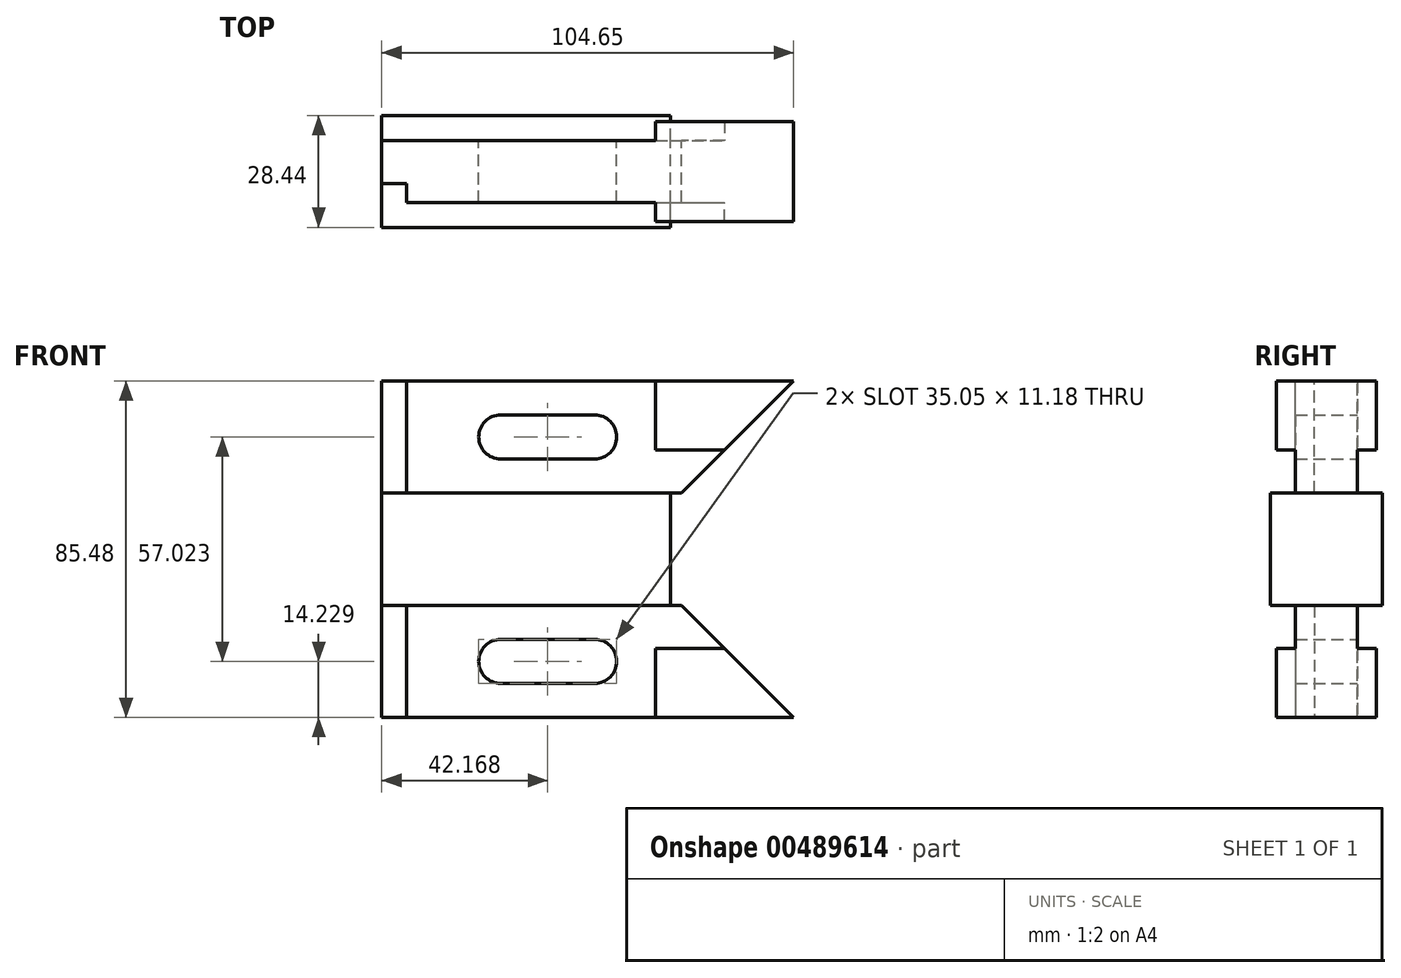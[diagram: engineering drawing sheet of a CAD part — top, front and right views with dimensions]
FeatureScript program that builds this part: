
annotation { "Feature Type Name" : "Feature", "Feature Type Description" : "" }
export const myFeature = defineFeature(function(context is Context, id is Id, definition is map)
    precondition{}
    {
        {
            var Q0;
            Q0=qCreatedBy(makeId("Front.planeOp"),FACE);
            var sketch = newSketch(context, id + "F0", { "sketchPlane" : qUnion([Q0])});
            skLineSegment(sketch, "E0.top", {"start": v(0, 14.29) * mm, "end": v(-73.4, 14.29) * mm});
            skLineSegment(sketch, "E1", {"start": v(-73.4, 14.29) * mm, "end": v(-73.4, 42.74) * mm});
            skLineSegment(sketch, "E2", {"start": v(-73.4, 42.74) * mm, "end": v(31.24, 42.74) * mm});
            skLineSegment(sketch, "E3", {"start": v(31.24, 42.74) * mm, "end": v(2.8, 14.29) * mm});
            skLineSegment(sketch, "E4", {"start": v(-67.06, 42.74) * mm, "end": v(-67.06, 14.29) * mm});
            skLineSegment(sketch, "E5", {"start": v(0, 14.29) * mm, "end": v(2.8, 14.29) * mm});
            skArc(sketch, "E6.0.startCap", {"start": v(-43.18, 22.92) * mm, "mid": v(-48.77, 28.51) * mm, "end": v(-43.18, 34.1) * mm});
            skArc(sketch, "E6.0.endCap", {"start": v(-19.3, 34.1) * mm, "mid": v(-13.72, 28.51) * mm, "end": v(-19.3, 22.92) * mm});
            skLineSegment(sketch, "E6.0.left", {"start": v(-43.18, 34.1) * mm, "end": v(-19.3, 34.1) * mm});
            skLineSegment(sketch, "E6.0.right", {"start": v(-43.18, 22.92) * mm, "end": v(-19.3, 22.92) * mm});
            skLineSegment(sketch, "E7", {"start": v(-48.77, 28.51) * mm, "end": v(-13.72, 28.51) * mm, "construction": true});
            skLineSegment(sketch, "E8", {"start": v(-73.4, 28.51) * mm, "end": v(-48.77, 28.51) * mm, "construction": true});
            skPoint(sketch, "E9", {"position": v(-67.06, 42.74) * mm});
            skPoint(sketch, "E10", {"position": v(-73.4, 42.74) * mm});
            skLineSegment(sketch, "E11.bottom", {"start": v(-73.4, 14.29) * mm, "end": v(0, 14.29) * mm});
            skLineSegment(sketch, "E11.top", {"start": v(-73.4, 0) * mm, "end": v(0, 0) * mm});
            skLineSegment(sketch, "E11.left", {"start": v(-73.4, 14.29) * mm, "end": v(-73.4, 0) * mm});
            skLineSegment(sketch, "E11.right", {"start": v(0, 14.29) * mm, "end": v(0, 0) * mm});
            skLineSegment(sketch, "E12", {"start": v(-73.4, 42.74) * mm, "end": v(-3.58, 42.74) * mm, "construction": true});
            skLineSegment(sketch, "E13", {"start": v(-3.58, 42.74) * mm, "end": v(-3.58, 25.2) * mm});
            skLineSegment(sketch, "E14", {"start": v(13.72, 25.2) * mm, "end": v(-3.58, 25.2) * mm});
            skSolve(sketch);
        }
        {
            var Q0;
            Q0 = qSketchRegion(id + "F0", true);
            extrude(context, id + "F1", {"entities" : qUnion([Q0]), "endBound" : BoundingType.SYMMETRIC, "depth" : 28.45 * mm});
        }
        {
            var Q0;
            Q0=makeQuery(id+"F1.opExtrude","SWEPT_FACE",FACE,{"disambiguationData":[OSD([sQuery(id+"F0.wireOp",EDGE,"E2")])]});
            var sketch = newSketch(context, id + "F2", { "sketchPlane" : qUnion([Q0])});
            skLineSegment(sketch, "E15.bottom", {"start": v(-73.4, 14.22) * mm, "end": v(-3.8, 14.22) * mm});
            skLineSegment(sketch, "E15.top", {"start": v(-73.4, 7.87) * mm, "end": v(-3.8, 7.87) * mm});
            skLineSegment(sketch, "E15.left", {"start": v(-73.4, 14.22) * mm, "end": v(-73.4, 7.87) * mm});
            skLineSegment(sketch, "E15.right", {"start": v(-3.8, 14.22) * mm, "end": v(-3.8, 7.87) * mm});
            skLineSegment(sketch, "E16.bottom", {"start": v(0, 14.22) * mm, "end": v(-3.8, 14.22) * mm});
            skLineSegment(sketch, "E16.top", {"start": v(0, 12.7) * mm, "end": v(-3.8, 12.7) * mm});
            skLineSegment(sketch, "E16.left", {"start": v(0, 14.22) * mm, "end": v(0, 12.7) * mm});
            skLineSegment(sketch, "E16.right", {"start": v(-3.8, 14.22) * mm, "end": v(-3.8, 12.7) * mm});
            skLineSegment(sketch, "E17.MirrorCS", {"start": v(0, -14.22) * mm, "end": v(0, -12.7) * mm});
            skLineSegment(sketch, "E18.MirrorCS", {"start": v(-3.8, -14.22) * mm, "end": v(-3.8, -12.7) * mm});
            skLineSegment(sketch, "E19.MirrorCS", {"start": v(-73.4, -14.22) * mm, "end": v(-3.8, -14.22) * mm});
            skLineSegment(sketch, "E20.MirrorCS", {"start": v(-73.4, -7.87) * mm, "end": v(-3.8, -7.87) * mm});
            skLineSegment(sketch, "E21.MirrorCS", {"start": v(-73.4, -14.22) * mm, "end": v(-73.4, -7.87) * mm});
            skLineSegment(sketch, "E22.MirrorCS", {"start": v(-3.8, -14.22) * mm, "end": v(-3.8, -7.87) * mm});
            skLineSegment(sketch, "E23.MirrorCS", {"start": v(0, -12.7) * mm, "end": v(-3.8, -12.7) * mm});
            skLineSegment(sketch, "E24.MirrorCS", {"start": v(0, -14.22) * mm, "end": v(-3.8, -14.22) * mm});
            skLineSegment(sketch, "E25.bottom", {"start": v(-73.4, -7.87) * mm, "end": v(-67.06, -7.87) * mm});
            skLineSegment(sketch, "E25.top", {"start": v(-73.4, -3.05) * mm, "end": v(-67.06, -3.05) * mm});
            skLineSegment(sketch, "E25.left", {"start": v(-73.4, -7.87) * mm, "end": v(-73.4, -3.05) * mm});
            skLineSegment(sketch, "E25.right", {"start": v(-67.06, -7.87) * mm, "end": v(-67.06, -3.05) * mm});
            skSolve(sketch);
        }
        {
            var Q0;
            Q0=makeQuery(id+"F1.opExtrude","SWEPT_FACE",FACE,{"disambiguationData":[OSD([sQuery(id+"F0.wireOp",EDGE,"E11.right")])]});
            var sketch = newSketch(context, id + "F3", { "sketchPlane" : qUnion([Q0])});
            skLineSegment(sketch, "E26.bottom", {"start": v(-14.22, 14.29) * mm, "end": v(-12.7, 14.29) * mm});
            skLineSegment(sketch, "E26.top", {"start": v(-14.22, 42.74) * mm, "end": v(-12.7, 42.74) * mm});
            skLineSegment(sketch, "E26.left", {"start": v(-14.22, 14.29) * mm, "end": v(-14.22, 42.74) * mm});
            skLineSegment(sketch, "E26.right", {"start": v(-12.7, 14.29) * mm, "end": v(-12.7, 42.74) * mm});
            skLineSegment(sketch, "E27.bottom", {"start": v(14.22, 14.29) * mm, "end": v(12.7, 14.29) * mm});
            skLineSegment(sketch, "E27.top", {"start": v(14.22, 42.74) * mm, "end": v(12.7, 42.74) * mm});
            skLineSegment(sketch, "E27.left", {"start": v(14.22, 14.29) * mm, "end": v(14.22, 42.74) * mm});
            skLineSegment(sketch, "E27.right", {"start": v(12.7, 14.29) * mm, "end": v(12.7, 42.74) * mm});
            skLineSegment(sketch, "E28", {"start": v(7.87, 25.2) * mm, "end": v(7.87, 14.29) * mm});
            skLineSegment(sketch, "E29", {"start": v(-7.87, 14.29) * mm, "end": v(-7.87, 25.2) * mm});
            skLineSegment(sketch, "E30.bottom", {"start": v(-12.7, 14.29) * mm, "end": v(-7.87, 14.29) * mm});
            skLineSegment(sketch, "E30.top", {"start": v(-12.7, 25.2) * mm, "end": v(-7.87, 25.2) * mm});
            skLineSegment(sketch, "E30.left", {"start": v(-12.7, 14.29) * mm, "end": v(-12.7, 25.2) * mm});
            skLineSegment(sketch, "E31.bottom", {"start": v(12.7, 14.29) * mm, "end": v(7.87, 14.29) * mm});
            skLineSegment(sketch, "E31.top", {"start": v(12.7, 25.2) * mm, "end": v(7.87, 25.2) * mm});
            skLineSegment(sketch, "E31.left", {"start": v(12.7, 14.29) * mm, "end": v(12.7, 25.2) * mm});
            skLineSegment(sketch, "E31.right", {"start": v(7.87, 14.29) * mm, "end": v(7.87, 25.2) * mm});
            skSolve(sketch);
        }
        {
            var Q0;
            Q0 = qSketchRegion(id + "F3", true);
            extrude(context, id + "F4", {"entities" : qUnion([Q0]), "operationType" : NewBodyOperationType.REMOVE, "endBound" : BoundingType.THROUGH_ALL, "oppositeDirection" : true, "depth" : 25.4 * mm, "hasSecondDirection" : true, "secondDirectionBound" : SecondDirectionBoundingType.THROUGH_ALL, "secondDirectionOppositeDirection" : false, "secondDirectionDepth" : 25.4 * mm});
        }
        {
            var Q0;
            Q0 = qSketchRegion(id + "F2", true);
            var Q1;
            Q1=makeQuery(id+"F4.boolean.opBoolean","COPY",FACE,{"derivedFrom":makeQuery(id+"F4.opExtrude","SWEPT_FACE",FACE,{"disambiguationData":[OSD([sQuery(id+"F3.wireOp",EDGE,"E26.bottom")])]})});
            extrude(context, id + "F5", {"entities" : qUnion([Q0]), "operationType" : NewBodyOperationType.REMOVE, "endBound" : BoundingType.UP_TO_SURFACE, "oppositeDirection" : true, "endBoundEntityFace" : qUnion([Q1]), "depth" : 25.4 * mm});
        }
        {
            var Q0;
            Q0=makeQuery(id+"F1.opExtrude","SWEPT_BODY",BODY,{"disambiguationData":[OSD([sQuery(id+"F0.wireOp",EDGE,"E1"),sQuery(id+"F0.wireOp",EDGE,"E2"),sQuery(id+"F0.wireOp",EDGE,"E3"),sQuery(id+"F0.wireOp",EDGE,"E5"),sQuery(id+"F0.wireOp",EDGE,"E6.0.startCap"),sQuery(id+"F0.wireOp",EDGE,"E6.0.endCap"),sQuery(id+"F0.wireOp",EDGE,"E6.0.left"),sQuery(id+"F0.wireOp",EDGE,"E6.0.right"),sQuery(id+"F0.wireOp",EDGE,"E11.top"),sQuery(id+"F0.wireOp",EDGE,"E11.left"),sQuery(id+"F0.wireOp",EDGE,"E11.right")])]});
            var Q1;
            Q1=qCreatedBy(makeId("Top.planeOp"),FACE);
            mirror(context, id + "F6", {"operationType" : NewBodyOperationType.ADD, "entities" : qUnion([Q0]), "mirrorPlane" : qUnion([Q1])});
        }
    });
